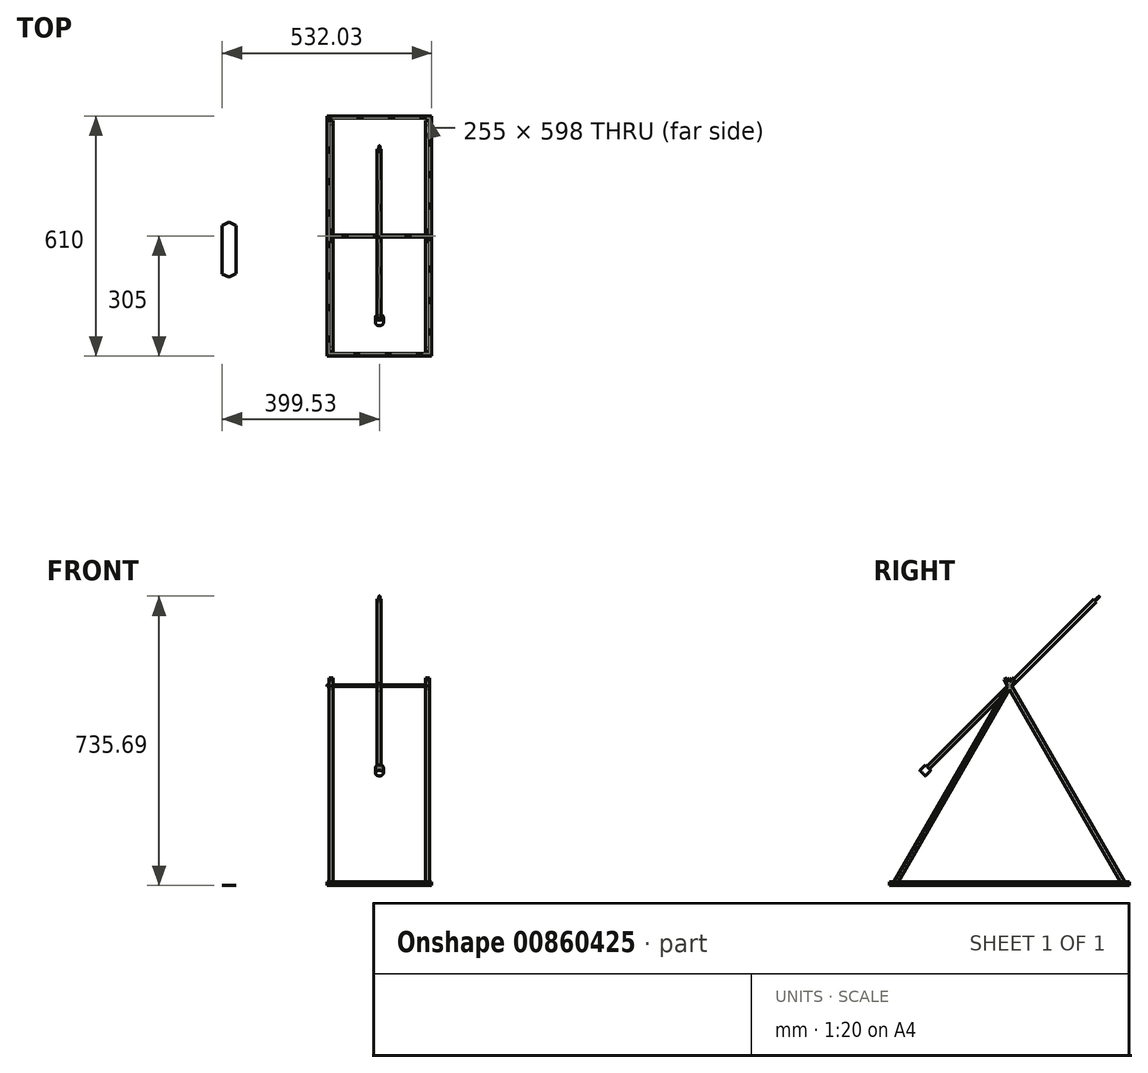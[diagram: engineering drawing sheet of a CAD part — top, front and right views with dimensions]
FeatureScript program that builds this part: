
annotation { "Feature Type Name" : "Feature", "Feature Type Description" : "" }
export const myFeature = defineFeature(function(context is Context, id is Id, definition is map)
    precondition{}
    {
        {
            var Q0;
            Q0=qCreatedBy(makeId("Top.planeOp"),FACE);
            var sketch = newSketch(context, id + "F0", { "sketchPlane" : qUnion([Q0])});
            skLineSegment(sketch, "E0.bottom", {"start": v(-132.5, 305) * mm, "end": v(132.5, 305) * mm});
            skLineSegment(sketch, "E0.top", {"start": v(-132.5, -305) * mm, "end": v(132.5, -305) * mm});
            skLineSegment(sketch, "E0.left", {"start": v(-132.5, 305) * mm, "end": v(-132.5, -305) * mm});
            skLineSegment(sketch, "E0.right", {"start": v(132.5, 305) * mm, "end": v(132.5, -305) * mm});
            skPoint(sketch, "E0.middle", {"position": v(0, 0) * mm});
            skSolve(sketch);
        }
        {
            var Q0;
            Q0=makeQuery(id+"F0.imprint","IMPRINT",FACE,{"disambiguationData":[TD([[makeQuery(id+"F0.imprint","IMPRINT",EDGE,{"derivedFrom":sQuery(id+"F0.wireOp",EDGE,"E0.bottom")}),-1.0]])]});
            extrude(context, id + "F1", {"entities" : qUnion([Q0]), "depth" : 10 * mm, "offsetDistance" : 25 * mm});
        }
        {
            var Q0;
            Q0=makeQuery(id+"F1.opExtrude","CAP_FACE",FACE,{"disambiguationData":[OSD([sQuery(id+"F0.wireOp",EDGE,"E0.bottom"),sQuery(id+"F0.wireOp",EDGE,"E0.top"),sQuery(id+"F0.wireOp",EDGE,"E0.left"),sQuery(id+"F0.wireOp",EDGE,"E0.right")])],"isStart":false});
            var sketch = newSketch(context, id + "F2", { "sketchPlane" : qUnion([Q0])});
            skLineSegment(sketch, "E1.bottom", {"start": v(-127.5, 299) * mm, "end": v(127.5, 299) * mm});
            skLineSegment(sketch, "E1.top", {"start": v(-127.5, -299) * mm, "end": v(127.5, -299) * mm});
            skLineSegment(sketch, "E1.left", {"start": v(-127.5, 299) * mm, "end": v(-127.5, -299) * mm});
            skLineSegment(sketch, "E1.right", {"start": v(127.5, 299) * mm, "end": v(127.5, -299) * mm});
            skPoint(sketch, "E1.middle", {"position": v(0, 0) * mm});
            skSolve(sketch);
        }
        {
            var Q0;
            Q0 = qSketchRegion(id + "F2", true);
            extrude(context, id + "F3", {"entities" : qUnion([Q0]), "operationType" : NewBodyOperationType.REMOVE, "oppositeDirection" : true, "depth" : 25 * mm, "offsetDistance" : 25 * mm});
        }
        {
            var Q0;
            Q0=makeQuery(id+"F3.boolean.opBoolean","COPY",FACE,{"derivedFrom":makeQuery(id+"F3.opExtrude","SWEPT_FACE",FACE,{"disambiguationData":[OSD([sQuery(id+"F2.wireOp",EDGE,"E1.left")])]})});
            var sketch = newSketch(context, id + "F4", { "sketchPlane" : qUnion([Q0])});
            skLineSegment(sketch, "E2", {"start": v(-299, 0) * mm, "end": v(6, 528.28) * mm});
            skLineSegment(sketch, "E3", {"start": v(6, 528.28) * mm, "end": v(14.66, 523.28) * mm});
            skLineSegment(sketch, "E4", {"start": v(-299, 0) * mm, "end": v(-290.34, -5) * mm});
            skLineSegment(sketch, "E5", {"start": v(14.66, 523.28) * mm, "end": v(-290.34, -5) * mm});
            skSolve(sketch);
        }
        {
            var Q0;
            {var subQ0=sQuery(id+"F4.wireOp",EDGE,"E3");Q0=makeQuery(id+"F4.imprint","IMPRINT",FACE,{"disambiguationData":[TD([[makeQuery(id+"F4.imprint","IMPRINT",EDGE,{"derivedFrom":subQ0}),-1.0]])]});}
            extrude(context, id + "F5", {"entities" : qUnion([Q0]), "depth" : 10 * mm, "offsetDistance" : 25 * mm});
        }
        {
            var Q0;
            Q0=makeQuery(id+"F5.opExtrude","SWEPT_BODY",BODY,{"disambiguationData":[OSD([sQuery(id+"F2.wireOp",EDGE,"E1.left"),sQuery(id+"F4.wireOp",EDGE,"E2"),sQuery(id+"F4.wireOp",EDGE,"E3"),sQuery(id+"F4.wireOp",EDGE,"E5")])]});
            var Q1;
            Q1=qCreatedBy(makeId("Right.planeOp"),FACE);
            mirror(context, id + "F6", {"entities" : qUnion([Q0]), "mirrorPlane" : qUnion([Q1])});
        }
        {
            var Q0;
            Q0=makeQuery(id+"F5.opExtrude","SWEPT_BODY",BODY,{"disambiguationData":[OSD([sQuery(id+"F2.wireOp",EDGE,"E1.left"),sQuery(id+"F4.wireOp",EDGE,"E2"),sQuery(id+"F4.wireOp",EDGE,"E3"),sQuery(id+"F4.wireOp",EDGE,"E5")])]});
            var Q1;
            Q1=makeQuery(id+"F6.opPattern","COPY",BODY,{"derivedFrom":makeQuery(id+"F5.opExtrude","SWEPT_BODY",BODY,{"disambiguationData":[OSD([sQuery(id+"F2.wireOp",EDGE,"E1.left"),sQuery(id+"F4.wireOp",EDGE,"E2"),sQuery(id+"F4.wireOp",EDGE,"E3"),sQuery(id+"F4.wireOp",EDGE,"E5")])]}),"instanceName":"1"});
            var Q2;
            Q2=qCreatedBy(makeId("Front.planeOp"),FACE);
            mirror(context, id + "F7", {"entities" : qUnion([Q0, Q1]), "mirrorPlane" : qUnion([Q2])});
        }
        {
            var Q0;
            Q0=makeQuery(id+"F6.opPattern","COPY",FACE,{"derivedFrom":makeQuery(id+"F5.opExtrude","CAP_FACE",FACE,{"disambiguationData":[OSD([sQuery(id+"F2.wireOp",EDGE,"E1.left"),sQuery(id+"F4.wireOp",EDGE,"E2"),sQuery(id+"F4.wireOp",EDGE,"E3"),sQuery(id+"F4.wireOp",EDGE,"E5")])],"isStart":true}),"instanceName":"1"});
            var sketch = newSketch(context, id + "F8", { "sketchPlane" : qUnion([Q0])});
            skCircle(sketch, "E6", {"center": v(0, 508.02) * mm, "radius": 2.5 * mm});
            skPoint(sketch, "E7", {"position": v(0, 497.88) * mm});
            skSolve(sketch);
        }
        {
            var Q0;
            Q0 = qSketchRegion(id + "F8", true);
            var Q1;
            Q1 = qConstructionFilter(qBodyType(qCreatedBy(id + "F8" ,EDGE), BodyType.WIRE), ConstructionObject.NO);
            extrude(context, id + "F9", {"entities" : qUnion([Q0]), "operationType" : NewBodyOperationType.ADD, "surfaceEntities" : qUnion([Q1]), "oppositeDirection" : true, "depth" : 260 * mm, "offsetDistance" : 25 * mm});
        }
        {
            var Q0;
            Q0=qCreatedBy(makeId("Top.planeOp"),FACE);
            var sketch = newSketch(context, id + "F10", { "sketchPlane" : qUnion([Q0])});
            skLineSegment(sketch, "E8.bottom", {"start": v(-5.7, 5.4) * mm, "end": v(4.3, 5.4) * mm});
            skLineSegment(sketch, "E8.top", {"start": v(-5.7, -4.6) * mm, "end": v(4.3, -4.6) * mm});
            skLineSegment(sketch, "E8.left", {"start": v(-5.7, 5.4) * mm, "end": v(-5.7, -4.6) * mm});
            skLineSegment(sketch, "E8.right", {"start": v(4.3, 5.4) * mm, "end": v(4.3, -4.6) * mm});
            skSolve(sketch);
        }
        {
            var Q0;
            Q0 = qSketchRegion(id + "F10", true);
            extrude(context, id + "F11", {"entities" : qUnion([Q0]), "depth" : 520 * mm, "offsetDistance" : 25 * mm});
        }
        {
            var Q0;
            Q0=makeQuery(id+"F11.opExtrude","CAP_EDGE",EDGE,{"disambiguationData":[OSD([sQuery(id+"F10.wireOp",EDGE,"E8.bottom")])],"isStart":false});
            chamfer(context, id + "F12", {"entities" : qUnion([Q0]), "width" : 15 * mm, "tangentPropagation" : true});
        }
        {
            var Q0;
            Q0=makeQuery(id+"F12.opChamfer","BLEND_FACE",FACE,{"disambiguationData":[OSD([sQuery(id+"F10.wireOp",EDGE,"E8.bottom")])]});
            var sketch = newSketch(context, id + "F13", { "sketchPlane" : qUnion([Q0])});
            skLineSegment(sketch, "E9.bottom", {"start": v(-4.3, 363.27) * mm, "end": v(5.7, 363.27) * mm});
            skLineSegment(sketch, "E9.top", {"start": v(-4.3, 353.27) * mm, "end": v(5.7, 353.27) * mm});
            skLineSegment(sketch, "E9.left", {"start": v(-4.3, 363.27) * mm, "end": v(-4.3, 353.27) * mm});
            skLineSegment(sketch, "E9.right", {"start": v(5.7, 363.27) * mm, "end": v(5.7, 353.27) * mm});
            skSolve(sketch);
        }
        {
            var Q0;
            Q0 = qSketchRegion(id + "F13", true);
            extrude(context, id + "F14", {"entities" : qUnion([Q0]), "endBound" : BoundingType.SYMMETRIC, "depth" : 610 * mm, "offsetDistance" : 25 * mm});
        }
        {
            var Q0;
            Q0=makeQuery(id+"F11.opExtrude","SWEPT_FACE",FACE,{"disambiguationData":[OSD([sQuery(id+"F10.wireOp",EDGE,"E8.right")])]});
            var sketch = newSketch(context, id + "F15", { "sketchPlane" : qUnion([Q0])});
            skLineSegment(sketch, "E10.bottom", {"start": v(5.4, 0) * mm, "end": v(-4.6, 0) * mm});
            skLineSegment(sketch, "E10.top", {"start": v(5.4, 478.3) * mm, "end": v(-4.6, 478.3) * mm});
            skLineSegment(sketch, "E10.left", {"start": v(5.4, 0) * mm, "end": v(5.4, 478.3) * mm});
            skLineSegment(sketch, "E10.right", {"start": v(-4.6, 0) * mm, "end": v(-4.6, 478.3) * mm});
            skSolve(sketch);
        }
        {
            var Q0;
            Q0=makeQuery(id+"F15.imprint","IMPRINT",FACE,{"disambiguationData":[TD([[makeQuery(id+"F15.imprint","IMPRINT",EDGE,{"derivedFrom":sQuery(id+"F15.wireOp",EDGE,"E10.bottom")}),-1.0]])]});
            extrude(context, id + "F16", {"entities" : qUnion([Q0]), "operationType" : NewBodyOperationType.REMOVE, "oppositeDirection" : true, "depth" : 25 * mm, "offsetDistance" : 25 * mm});
        }
        {
            var Q0;
            Q0=makeQuery(id+"F11.opExtrude","SWEPT_FACE",FACE,{"disambiguationData":[OSD([sQuery(id+"F10.wireOp",EDGE,"E8.right")])]});
            var sketch = newSketch(context, id + "F17", { "sketchPlane" : qUnion([Q0])});
            skLineSegment(sketch, "E11", {"start": v(5.4, 505) * mm, "end": v(-4.6, 495) * mm});
            skLineSegment(sketch, "E12", {"start": v(-4.6, 495) * mm, "end": v(-4.6, 478.3) * mm});
            skLineSegment(sketch, "E13", {"start": v(-4.6, 478.3) * mm, "end": v(5.4, 478.3) * mm});
            skLineSegment(sketch, "E14", {"start": v(5.4, 478.3) * mm, "end": v(5.4, 505) * mm});
            skSolve(sketch);
        }
        {
            var Q0;
            Q0 = qSketchRegion(id + "F17", true);
            extrude(context, id + "F18", {"entities" : qUnion([Q0]), "operationType" : NewBodyOperationType.REMOVE, "oppositeDirection" : true, "depth" : 25 * mm, "offsetDistance" : 25 * mm});
        }
        {
            var Q0;
            Q0=makeQuery(id+"F11.opExtrude","SWEPT_FACE",FACE,{"disambiguationData":[OSD([sQuery(id+"F10.wireOp",EDGE,"E8.right")])]});
            var sketch = newSketch(context, id + "F19", { "sketchPlane" : qUnion([Q0])});
            skLineSegment(sketch, "E15", {"start": v(-4.6, 520) * mm, "end": v(-4.6, 511.83) * mm});
            skLineSegment(sketch, "E16", {"start": v(-4.6, 511.83) * mm, "end": v(3.57, 520) * mm});
            skLineSegment(sketch, "E17", {"start": v(3.57, 520) * mm, "end": v(-4.6, 520) * mm});
            skSolve(sketch);
        }
        {
            var Q0;
            Q0 = qSketchRegion(id + "F19", true);
            extrude(context, id + "F20", {"entities" : qUnion([Q0]), "operationType" : NewBodyOperationType.REMOVE, "oppositeDirection" : true, "depth" : 25 * mm, "offsetDistance" : 25 * mm});
        }
        {
            var Q0;
            Q0=makeQuery(id+"F14.opExtrude","CAP_FACE",FACE,{"disambiguationData":[OSD([sQuery(id+"F13.wireOp",EDGE,"E9.bottom"),sQuery(id+"F13.wireOp",EDGE,"E9.top"),sQuery(id+"F13.wireOp",EDGE,"E9.left"),sQuery(id+"F13.wireOp",EDGE,"E9.right")])],"isStart":false});
            var sketch = newSketch(context, id + "F21", { "sketchPlane" : qUnion([Q0])});
            skCircle(sketch, "E18", {"center": v(0, 358.27) * mm, "radius": 1.25 * mm});
            skPoint(sketch, "E18.centerSnap0", {"position": v(-4.3, 358.27) * mm});
            skSolve(sketch);
        }
        {
            var Q0;
            Q0=makeQuery(id+"F14.opExtrude","CAP_FACE",FACE,{"disambiguationData":[OSD([sQuery(id+"F13.wireOp",EDGE,"E9.bottom"),sQuery(id+"F13.wireOp",EDGE,"E9.top"),sQuery(id+"F13.wireOp",EDGE,"E9.left"),sQuery(id+"F13.wireOp",EDGE,"E9.right")])],"isStart":true});
            var sketch = newSketch(context, id + "F22", { "sketchPlane" : qUnion([Q0])});
            skCircle(sketch, "E19", {"center": v(0, 358.27) * mm, "radius": 10 * mm});
            skPoint(sketch, "E19.centerSnap0", {"position": v(4.3, 358.27) * mm});
            skSolve(sketch);
        }
        {
            var Q0;
            Q0 = qSketchRegion(id + "F22", true);
            extrude(context, id + "F23", {"entities" : qUnion([Q0]), "operationType" : NewBodyOperationType.ADD, "endBound" : BoundingType.SYMMETRIC, "depth" : 20 * mm, "offsetDistance" : 25 * mm});
        }
        {
            var Q0;
            Q0=makeQuery(id+"F21.imprint","IMPRINT",FACE,{"disambiguationData":[TD([[makeQuery(id+"F21.imprint","IMPRINT",EDGE,{"derivedFrom":sQuery(id+"F21.wireOp",EDGE,"E18")}),1.0]])]});
            extrude(context, id + "F24", {"entities" : qUnion([Q0]), "operationType" : NewBodyOperationType.ADD, "depth" : 15 * mm, "offsetDistance" : 25 * mm});
        }
        {
            var Q0;
            Q0=qCreatedBy(makeId("Top.planeOp"),FACE);
            var sketch = newSketch(context, id + "F25", { "sketchPlane" : qUnion([Q0])});
            skLineSegment(sketch, "E20", {"start": v(-399.53, 20.41) * mm, "end": v(-399.53, -89.9) * mm});
            skLineSegment(sketch, "E21", {"start": v(-363.7, -90.85) * mm, "end": v(-363.7, 17.7) * mm});
            skLineSegment(sketch, "E22", {"start": v(-381.6, -104.49) * mm, "end": v(-400.02, -96.67) * mm});
            skLineSegment(sketch, "E23", {"start": v(-381.6, -104.49) * mm, "end": v(-363.7, -95.53) * mm});
            skLineSegment(sketch, "E24", {"start": v(-381.62, 35.35) * mm, "end": v(-399.53, 26.4) * mm});
            skLineSegment(sketch, "E25", {"start": v(-381.62, 35.35) * mm, "end": v(-363.72, 26.2) * mm});
            skLineSegment(sketch, "E26", {"start": v(-399.53, 20.41) * mm, "end": v(-399.53, 26.4) * mm});
            skLineSegment(sketch, "E27", {"start": v(-363.72, 26.2) * mm, "end": v(-363.7, 17.7) * mm});
            skLineSegment(sketch, "E28", {"start": v(-399.53, -89.9) * mm, "end": v(-399.53, -96.88) * mm});
            skLineSegment(sketch, "E29", {"start": v(-363.7, -90.85) * mm, "end": v(-363.7, -95.53) * mm});
            skSolve(sketch);
        }
        {
            var Q0;
            Q0 = qSketchRegion(id + "F25", true);
            extrude(context, id + "F26", {"entities" : qUnion([Q0]), "depth" : 1 * mm, "offsetDistance" : 25 * mm});
        }
    });
